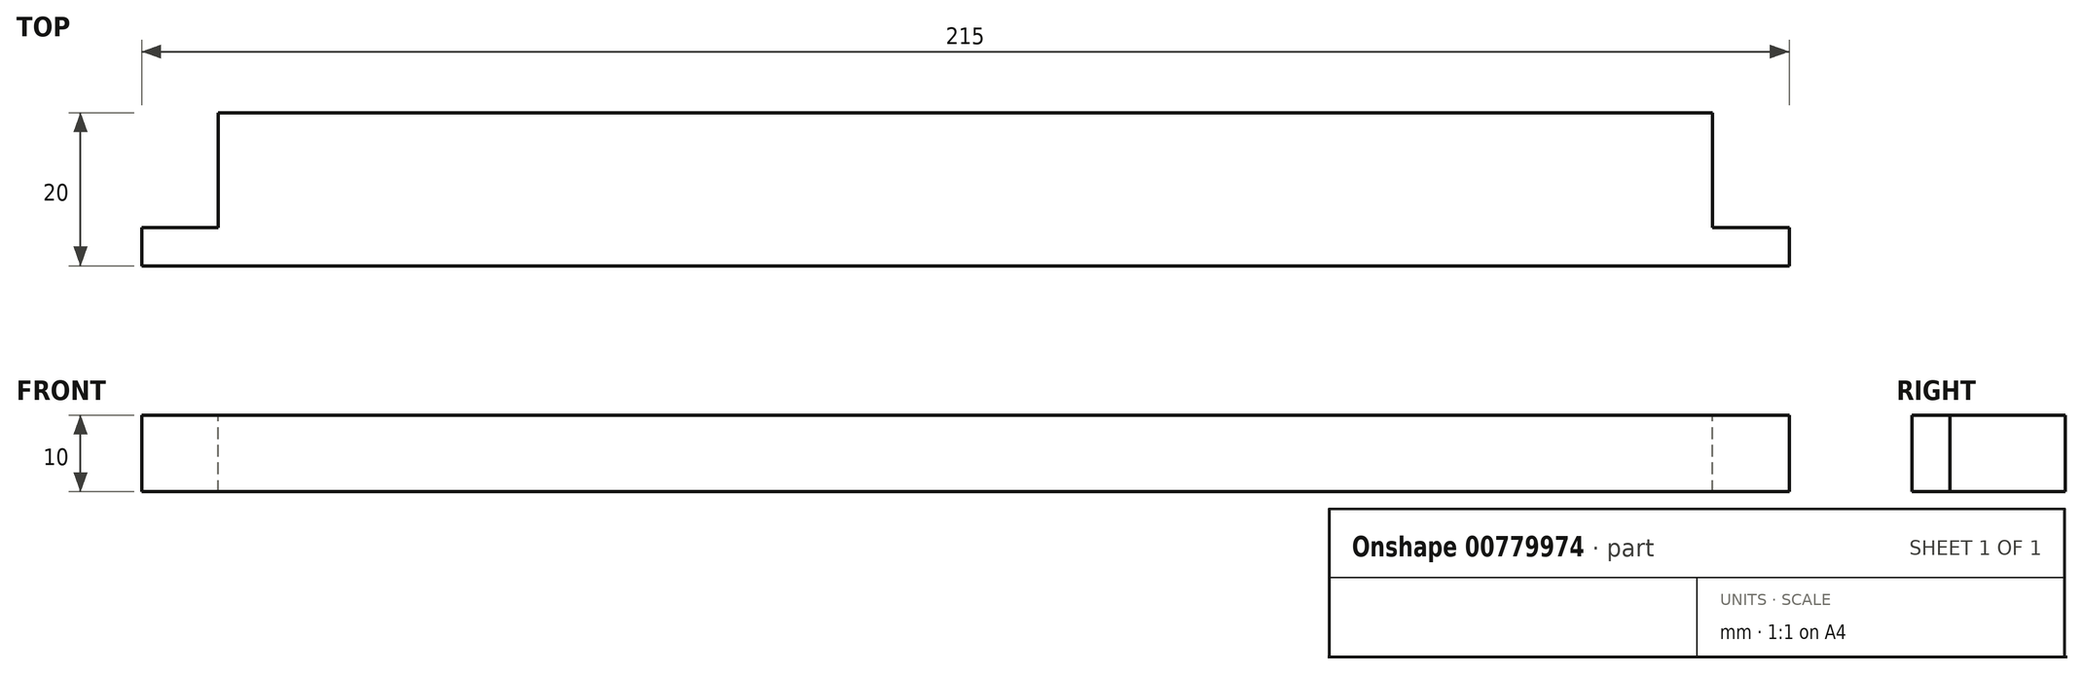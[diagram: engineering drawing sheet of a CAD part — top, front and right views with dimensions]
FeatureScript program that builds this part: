
annotation { "Feature Type Name" : "Feature", "Feature Type Description" : "" }
export const myFeature = defineFeature(function(context is Context, id is Id, definition is map)
    precondition{}
    {
        {
            var Q0;
            Q0=qCreatedBy(makeId("Top.planeOp"),FACE);
            var sketch = newSketch(context, id + "F0", { "sketchPlane" : qUnion([Q0])});
            skLineSegment(sketch, "E0", {"start": v(0, 0) * mm, "end": v(0, 20) * mm});
            skLineSegment(sketch, "E1", {"start": v(0, 20) * mm, "end": v(215, 20) * mm});
            skLineSegment(sketch, "E2", {"start": v(215, 20) * mm, "end": v(215, 0) * mm});
            skLineSegment(sketch, "E3", {"start": v(215, 0) * mm, "end": v(0, 0) * mm});
            skSolve(sketch);
        }
        {
            var Q0;
            Q0 = qSketchRegion(id + "F0", true);
            extrude(context, id + "F1", {"entities" : qUnion([Q0]), "depth" : 10 * mm, "offsetDistance" : 25 * mm});
        }
        {
            var Q0;
            Q0=makeQuery(id+"F1.opExtrude","CAP_FACE",FACE,{"disambiguationData":[OSD([sQuery(id+"F0.wireOp",EDGE,"E0"),sQuery(id+"F0.wireOp",EDGE,"E1"),sQuery(id+"F0.wireOp",EDGE,"E2"),sQuery(id+"F0.wireOp",EDGE,"E3")])],"isStart":false});
            var sketch = newSketch(context, id + "F2", { "sketchPlane" : qUnion([Q0])});
            skLineSegment(sketch, "E4", {"start": v(0, 5) * mm, "end": v(10, 5) * mm});
            skLineSegment(sketch, "E5", {"start": v(10, 5) * mm, "end": v(10, 20) * mm});
            skLineSegment(sketch, "E6", {"start": v(0, 10) * mm, "end": v(10, 10) * mm});
            skLineSegment(sketch, "E7", {"start": v(215, 5) * mm, "end": v(205, 5) * mm});
            skLineSegment(sketch, "E8", {"start": v(205, 5) * mm, "end": v(205, 20) * mm});
            skLineSegment(sketch, "E9", {"start": v(215, 10) * mm, "end": v(205, 10) * mm});
            skLineSegment(sketch, "E10", {"start": v(0, 5) * mm, "end": v(0, 20) * mm});
            skLineSegment(sketch, "E11", {"start": v(0, 20) * mm, "end": v(10, 20) * mm});
            skLineSegment(sketch, "E12", {"start": v(205, 20) * mm, "end": v(215, 20) * mm});
            skLineSegment(sketch, "E13", {"start": v(215, 20) * mm, "end": v(215, 5) * mm});
            skSolve(sketch);
        }
        {
            var Q0;
            Q0 = qSketchRegion(id + "F2", true);
            extrude(context, id + "F3", {"entities" : qUnion([Q0]), "operationType" : NewBodyOperationType.REMOVE, "endBound" : BoundingType.THROUGH_ALL, "oppositeDirection" : true, "depth" : 25 * mm, "offsetDistance" : 25 * mm});
        }
    });
